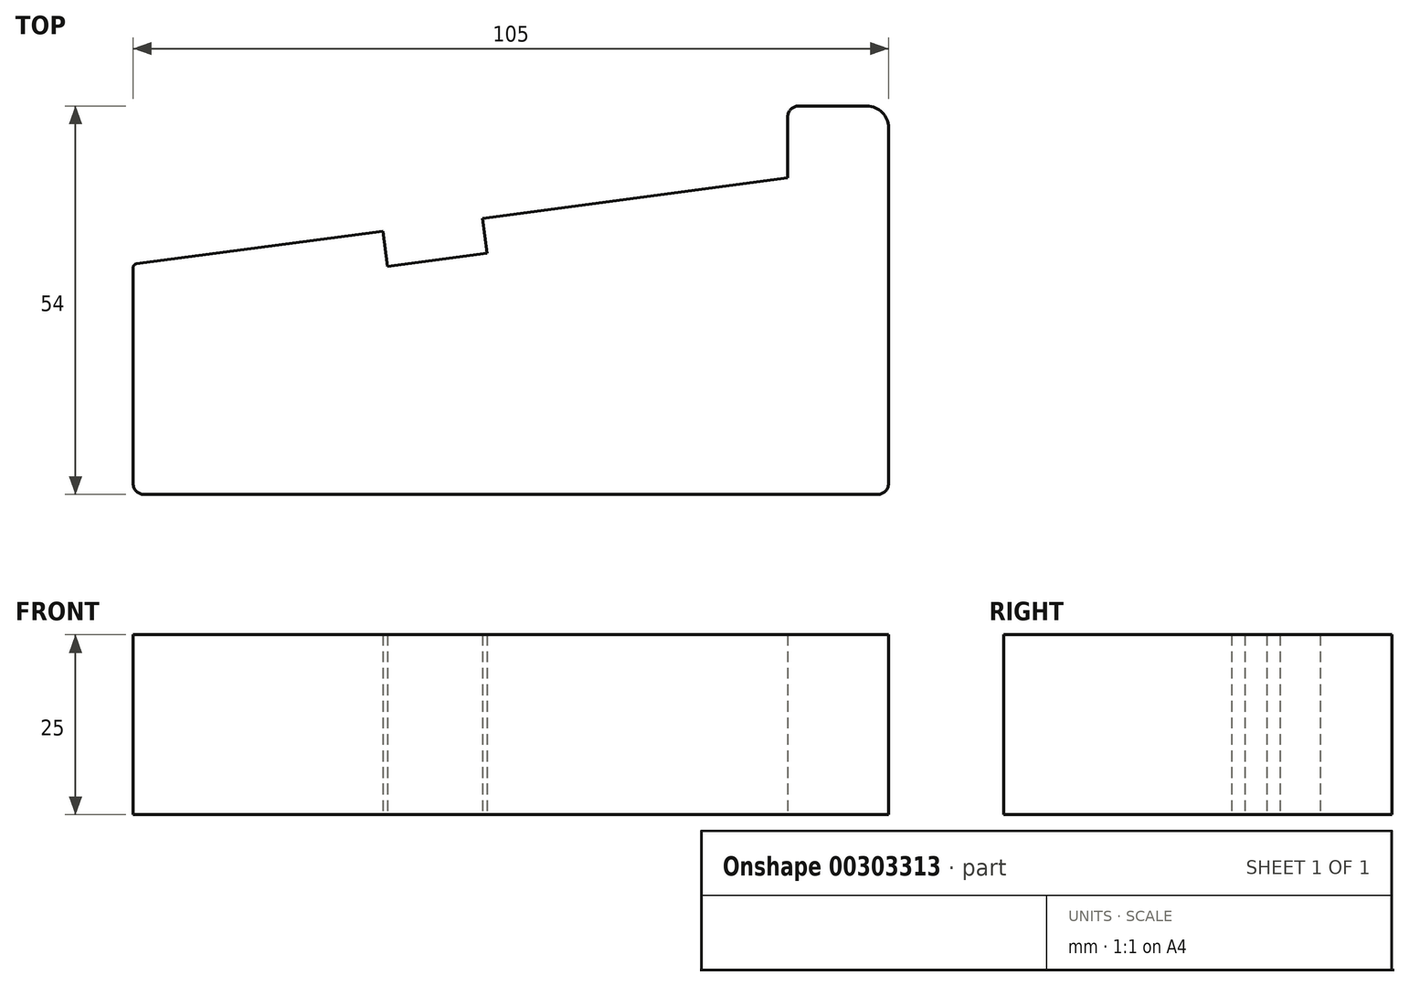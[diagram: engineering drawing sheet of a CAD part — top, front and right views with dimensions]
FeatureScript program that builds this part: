
annotation { "Feature Type Name" : "Feature", "Feature Type Description" : "" }
export const myFeature = defineFeature(function(context is Context, id is Id, definition is map)
    precondition{}
    {
        {
            var Q0;
            Q0=qCreatedBy(makeId("Top.planeOp"),FACE);
            var sketch = newSketch(context, id + "F0", { "sketchPlane" : qUnion([Q0])});
            skLineSegment(sketch, "E0", {"start": v(-84.29, 0) * mm, "end": v(17.71, 0) * mm});
            skLineSegment(sketch, "E1", {"start": v(19.21, 1.5) * mm, "end": v(19.21, 51) * mm});
            skLineSegment(sketch, "E2", {"start": v(16.21, 54) * mm, "end": v(6.71, 54) * mm});
            skLineSegment(sketch, "E3", {"start": v(5.21, 52.5) * mm, "end": v(5.21, 44) * mm});
            skLineSegment(sketch, "E4", {"start": v(-85.79, 1.5) * mm, "end": v(-85.79, 31.56) * mm});
            skLineSegment(sketch, "E5", {"start": v(-85.79, 32) * mm, "end": v(-51.09, 36.58) * mm});
            skLineSegment(sketch, "E6", {"start": v(-85.35, 32.06) * mm, "end": v(-51.09, 36.58) * mm});
            skLineSegment(sketch, "E7", {"start": v(-51.09, 36.58) * mm, "end": v(-50.45, 31.73) * mm});
            skLineSegment(sketch, "E8", {"start": v(-50.45, 31.73) * mm, "end": v(-36.57, 33.56) * mm});
            skLineSegment(sketch, "E9", {"start": v(-36.57, 33.56) * mm, "end": v(-37.2, 38.4) * mm});
            skLineSegment(sketch, "E10.trimOffspring", {"start": v(-37.2, 38.4) * mm, "end": v(5.21, 44) * mm});
            skPoint(sketch, "E11.visualSharp", {"position": v(5.21, 54) * mm});
            skArc(sketch, "E11.filletArc", {"start": v(6.71, 54) * mm, "mid": v(5.65, 53.56) * mm, "end": v(5.21, 52.5) * mm});
            skPoint(sketch, "E12.visualSharp", {"position": v(19.21, 54) * mm});
            skArc(sketch, "E12.filletArc", {"start": v(19.21, 51) * mm, "mid": v(18.33, 53.12) * mm, "end": v(16.21, 54) * mm});
            skPoint(sketch, "E13.visualSharp", {"position": v(-85.79, 32) * mm});
            skArc(sketch, "E13.filletArc", {"start": v(-85.35, 32.06) * mm, "mid": v(-85.66, 31.9) * mm, "end": v(-85.79, 31.56) * mm});
            skPoint(sketch, "E14.visualSharp", {"position": v(-85.79, 0) * mm});
            skArc(sketch, "E14.filletArc", {"start": v(-85.79, 1.5) * mm, "mid": v(-85.35, 0.44) * mm, "end": v(-84.29, 0) * mm});
            skPoint(sketch, "E15.visualSharp", {"position": v(19.21, 0) * mm});
            skArc(sketch, "E15.filletArc", {"start": v(17.71, 0) * mm, "mid": v(18.77, 0.44) * mm, "end": v(19.21, 1.5) * mm});
            skSolve(sketch);
        }
        {
            var Q0;
            Q0=makeQuery(id+"F0.imprint","IMPRINT",FACE,{"disambiguationData":[TD([[makeQuery(id+"F0.imprint","IMPRINT",EDGE,{"derivedFrom":sQuery(id+"F0.wireOp",EDGE,"E0")}),1.0]])]});
            extrude(context, id + "F1", {"entities" : qUnion([Q0]), "depth" : 25 * mm});
        }
    });
